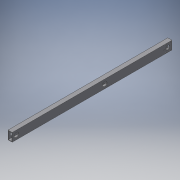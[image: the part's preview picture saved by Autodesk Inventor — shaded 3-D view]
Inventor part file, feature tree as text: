
AUTODESK INVENTOR PART (.ipt)
format: ipt  version: 2018 (Build 220112000, 112)  size: 167,936 bytes
history: native  units: in
note: dims shown in document units (in); Inventor stores cm internally (conversion verified against a paired STEP export)
features: extrude x6, sketch x6
ambient origin geometry x8: Origin, YZ Plane, XZ Plane, XY Plane, X Axis, Y Axis, Z Axis, Center Point
bodies: Solid1 (feature_tree)
feature tree (12):
  extrude  "Extrusion1"  Depth=2.0in
  extrude  "Extrusion2"  Depth=38.0in TaperAngle=0.0deg
  extrude  "Extrusion3"  Depth=1.0in TaperAngle=0.0deg
  extrude  "Extrusion4"  Depth=1.0in
  extrude  "Extrusion5"  Depth=1.0in TaperAngle=0.0deg
  extrude  "Extrusion6"  Depth=1.0in
  sketch  "Sketch1"  dims[d0=1.0in d1=2.0in]
  sketch  "Sketch2"  dims[d2=0.125in d3=38.0in d4=0.0in]
  sketch  "Sketch3"  dims[d5=1.0in d7=10.0in d8=0.0in]
  sketch  "Sketch4"  dims[d9=1.0in d10=7.0in]
  sketch  "Sketch5"  dims[d11=1.125in d12=1.0in d13=0.0in]
  sketch  "Sketch6"  dims[d14=22.0in d15=1.125in d16=1.0in d17=0.0in d18=1.0in d19=135.0deg d20=1.0in d21=0.16in d22=0.16in d23=1.0in d24=0.0in d25=1.0in d26=1.875in d27=0.2031in d28=0.2031in d29=0.2031in d30=0.2031in d31=0.2031in d32=1.0in d33=0.0in]
